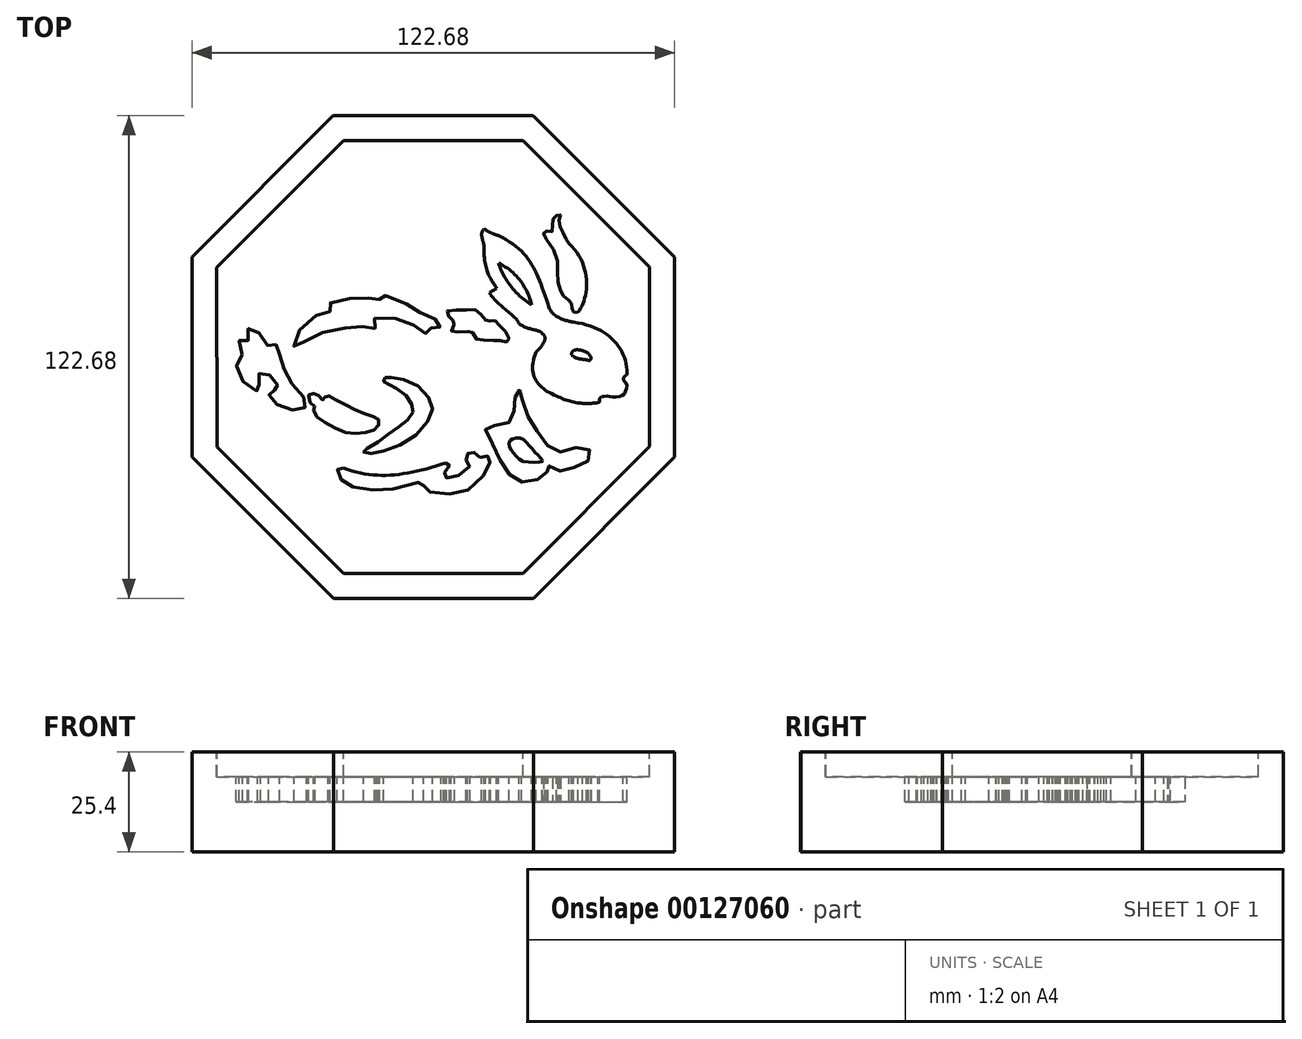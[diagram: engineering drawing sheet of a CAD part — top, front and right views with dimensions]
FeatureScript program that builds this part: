
annotation { "Feature Type Name" : "Feature", "Feature Type Description" : "" }
export const myFeature = defineFeature(function(context is Context, id is Id, definition is map)
    precondition{}
    {
        {
            var Q0;
            Q0=qCreatedBy(makeId("Top.planeOp"),FACE);
            var sketch = newSketch(context, id + "F0", { "sketchPlane" : qUnion([Q0])});
            skCircle(sketch, "E0.cCircle", {"center": v(0, 0) * mm, "radius": 61.32 * mm, "construction": true});
            skLineSegment(sketch, "E0.0", {"start": v(-61.3, -25.44) * mm, "end": v(-61.34, 25.36) * mm});
            skLineSegment(sketch, "E0.1", {"start": v(-61.34, 25.36) * mm, "end": v(-25.44, 61.3) * mm});
            skLineSegment(sketch, "E0.2", {"start": v(-25.44, 61.3) * mm, "end": v(25.36, 61.34) * mm});
            skLineSegment(sketch, "E0.3", {"start": v(25.36, 61.34) * mm, "end": v(61.3, 25.44) * mm});
            skLineSegment(sketch, "E0.4", {"start": v(61.3, 25.44) * mm, "end": v(61.34, -25.36) * mm});
            skLineSegment(sketch, "E0.5", {"start": v(61.34, -25.36) * mm, "end": v(25.44, -61.3) * mm});
            skLineSegment(sketch, "E0.6", {"start": v(25.44, -61.3) * mm, "end": v(-25.36, -61.34) * mm});
            skLineSegment(sketch, "E0.7", {"start": v(-25.36, -61.34) * mm, "end": v(-61.3, -25.44) * mm});
            skPoint(sketch, "E0.0.midPoint", {"position": v(-61.32, -0.04) * mm});
            skSolve(sketch);
        }
        {
            var Q0;
            Q0=qSketchRegion(id+"F0",true);
            extrude(context, id + "F1", {"entities" : qUnion([Q0]), "depth" : 25.4 * mm});
        }
        {
            var Q0;
            Q0=makeQuery(id+"F1.opExtrude","CAP_FACE",FACE,{"disambiguationData":[OSD([sQuery(id+"F0.wireOp",EDGE,"E0.0"),sQuery(id+"F0.wireOp",EDGE,"E0.1"),sQuery(id+"F0.wireOp",EDGE,"E0.2"),sQuery(id+"F0.wireOp",EDGE,"E0.3"),sQuery(id+"F0.wireOp",EDGE,"E0.4"),sQuery(id+"F0.wireOp",EDGE,"E0.5"),sQuery(id+"F0.wireOp",EDGE,"E0.6"),sQuery(id+"F0.wireOp",EDGE,"E0.7")])],"isStart":false});
            var sketch = newSketch(context, id + "F2", { "sketchPlane" : qUnion([Q0])});
            skLineSegment(sketch, "E1.0", {"start": v(-54.96, -22.8) * mm, "end": v(-54.99, 22.73) * mm});
            skLineSegment(sketch, "E1.1", {"start": v(-22.73, -54.99) * mm, "end": v(-54.96, -22.8) * mm});
            skLineSegment(sketch, "E1.2", {"start": v(-54.99, 22.73) * mm, "end": v(-22.8, 54.96) * mm});
            skLineSegment(sketch, "E1.3", {"start": v(22.8, -54.96) * mm, "end": v(-22.73, -54.99) * mm});
            skLineSegment(sketch, "E1.4", {"start": v(-22.8, 54.96) * mm, "end": v(22.73, 54.99) * mm});
            skLineSegment(sketch, "E1.5", {"start": v(22.73, 54.99) * mm, "end": v(54.96, 22.8) * mm});
            skLineSegment(sketch, "E1.6", {"start": v(54.96, 22.8) * mm, "end": v(54.99, -22.73) * mm});
            skLineSegment(sketch, "E1.7", {"start": v(54.99, -22.73) * mm, "end": v(22.8, -54.96) * mm});
            skSolve(sketch);
        }
        {
            var Q0;
            Q0=qSketchRegion(id+"F2",true);
            extrude(context, id + "F3", {"entities" : qUnion([Q0]), "operationType" : NewBodyOperationType.REMOVE, "oppositeDirection" : true, "depth" : 6.35 * mm});
        }
        {
            var Q0;
            Q0=makeQuery(id+"F3.boolean.opBoolean","COPY",FACE,{"derivedFrom":makeQuery(id+"F3.opExtrude","CAP_FACE",FACE,{"disambiguationData":[OSD([sQuery(id+"F2.wireOp",EDGE,"E1.0"),sQuery(id+"F2.wireOp",EDGE,"E1.1"),sQuery(id+"F2.wireOp",EDGE,"E1.2"),sQuery(id+"F2.wireOp",EDGE,"E1.3"),sQuery(id+"F2.wireOp",EDGE,"E1.4"),sQuery(id+"F2.wireOp",EDGE,"E1.5"),sQuery(id+"F2.wireOp",EDGE,"E1.6"),sQuery(id+"F2.wireOp",EDGE,"E1.7")])],"isStart":false})});
            var sketch = newSketch(context, id + "F4", { "sketchPlane" : qUnion([Q0])});
            skFitSpline(sketch, "E2", {"points": [v(16.6, 23.85) * mm, v(25, 13.25) * mm], "startDerivative": vector(13.68, -6.4) * mm, "endDerivative": vector(3.38, -13.15) * mm});
            skFitSpline(sketch, "E3", {"points": [v(16.6, 23.85) * mm, v(25, 13.25) * mm], "startDerivative": vector(3.38, -11.2) * mm, "endDerivative": vector(12.61, -7.28) * mm});
            skFitSpline(sketch, "E4", {"points": [v(12.87, 32.6) * mm, v(16.54, 30.9) * mm], "startDerivative": vector(4.26, -2.66) * mm, "endDerivative": vector(3.55, -0.53) * mm});
            skFitSpline(sketch, "E5", {"points": [v(16.54, 30.9) * mm, v(29.1, 13.42) * mm], "startDerivative": vector(24.52, -12.44) * mm, "endDerivative": vector(8.7, -26.3) * mm});
            skFitSpline(sketch, "E6", {"points": [v(29.1, 13.42) * mm, v(35.6, 8.86) * mm], "startDerivative": vector(2.49, -10.13) * mm, "endDerivative": vector(6.93, -1.42) * mm});
            skFitSpline(sketch, "E7", {"points": [v(12.87, 32.6) * mm, v(12.87, 28.05) * mm], "startDerivative": vector(-3.9, -4.62) * mm, "endDerivative": vector(0, -4.56) * mm});
            skFitSpline(sketch, "E8", {"points": [v(12.87, 28.05) * mm, v(16.12, 17.45) * mm], "startDerivative": vector(0, -19) * mm, "endDerivative": vector(5.33, -8.35) * mm});
            skFitSpline(sketch, "E9", {"points": [v(16.12, 17.45) * mm, v(14.23, 16.38) * mm], "startDerivative": vector(-1.9, -1.07) * mm, "endDerivative": vector(-1.9, -1.07) * mm});
            skFitSpline(sketch, "E10", {"points": [v(14.23, 16.38) * mm, v(21.8, 8.5) * mm], "startDerivative": vector(6.57, -10.84) * mm, "endDerivative": vector(3.38, -7.28) * mm});
            skFitSpline(sketch, "E11", {"points": [v(21.8, 8.5) * mm, v(27.6, 5.96) * mm], "startDerivative": vector(5.5, -4.97) * mm, "endDerivative": vector(0.36, -3.02) * mm});
            skFitSpline(sketch, "E12", {"points": [v(27.6, 5.96) * mm, v(26.13, 1.28) * mm], "startDerivative": vector(3.38, -1.78) * mm, "endDerivative": vector(-8.35, -8) * mm});
            skFitSpline(sketch, "E13", {"points": [v(26.13, 1.28) * mm, v(31.28, -9.85) * mm], "startDerivative": vector(-7.28, -16.88) * mm, "endDerivative": vector(14.74, -5.68) * mm});
            skFitSpline(sketch, "E14", {"points": [v(35.6, 8.86) * mm, v(49.25, -4.16) * mm], "startDerivative": vector(27.07, -3.62) * mm, "endDerivative": vector(0.36, -19.2) * mm});
            skFitSpline(sketch, "E15", {"points": [v(31.28, -9.85) * mm, v(41.9, -11.58) * mm], "startDerivative": vector(11.45, -6.22) * mm, "endDerivative": vector(9.7, 1.41) * mm});
            skFitSpline(sketch, "E16", {"points": [v(41.9, -11.58) * mm, v(42.28, -11.32) * mm, v(42.12, -10.92) * mm, v(42.4, -10.35) * mm, v(42.97, -10.04) * mm, v(44.26, -9.98) * mm, v(46.05, -10.13) * mm, v(48.08, -9.76) * mm, v(49, -8.44) * mm, v(49.15, -6.87) * mm, v(48.37, -5.9) * mm, v(48.33, -5.2) * mm, v(48.9, -4.67) * mm, v(49.25, -4.16) * mm], "startDerivative": vector(10.5, 4.13) * mm, "endDerivative": vector(4.68, 8.85) * mm});
            skFitSpline(sketch, "E17", {"points": [v(35.16, 0.47) * mm, v(37.86, 1.66) * mm], "startDerivative": vector(-0.47, 4.33) * mm, "endDerivative": vector(4.52, -1.22) * mm});
            skFitSpline(sketch, "E18", {"points": [v(37.86, 1.66) * mm, v(39.43, -0.85) * mm], "startDerivative": vector(8.19, -2.54) * mm, "endDerivative": vector(-2.82, 0.75) * mm});
            skFitSpline(sketch, "E19", {"points": [v(35.16, 0.47) * mm, v(39.43, -0.85) * mm], "startDerivative": vector(3.39, -3.58) * mm, "endDerivative": vector(2.26, -0.94) * mm});
            skFitSpline(sketch, "E20", {"points": [v(36.78, 11.4) * mm, v(34.5, 28.77) * mm], "startDerivative": vector(8.06, 10.18) * mm, "endDerivative": vector(-18.13, 16.56) * mm});
            skFitSpline(sketch, "E21", {"points": [v(36.78, 11.4) * mm, v(36, 11.4) * mm, v(35.58, 11.4) * mm, v(35.17, 12.62) * mm, v(35.1, 13.63) * mm, v(34.61, 14.34) * mm, v(33.23, 15.34) * mm, v(32.26, 17.06) * mm, v(31.52, 20.83) * mm, v(31.1, 26.16) * mm, v(28.12, 30.94) * mm, v(28.12, 31.65) * mm, v(28.87, 32.02) * mm, v(30.1, 31.83) * mm, v(30.25, 33.62) * mm, v(30.47, 35.12) * mm, v(31.22, 35.94) * mm, v(32.23, 36.2) * mm, v(32.08, 35.53) * mm, v(32.08, 33.74) * mm, v(32.71, 32.06) * mm, v(33.76, 30) * mm, v(34.5, 28.77) * mm], "startDerivative": vector(-23.61, 2.15) * mm, "endDerivative": vector(16.72, -26.25) * mm});
            skFitSpline(sketch, "E22", {"points": [v(15.3, 4.19) * mm, v(16.63, 4.28) * mm, v(18.23, 3.85) * mm, v(18.92, 4.02) * mm, v(19.22, 4.68) * mm, v(18.4, 6.51) * mm, v(16.63, 8.24) * mm, v(15.73, 9.2) * mm, v(14.87, 9.34) * mm, v(14, 8.97) * mm, v(13.2, 9.44) * mm, v(12.28, 10.6) * mm, v(10.65, 12) * mm, v(8.29, 11.96) * mm, v(4.67, 11.9) * mm, v(3.34, 11.5) * mm, v(4, 10.17) * mm, v(4.93, 9.27) * mm, v(5.43, 8.74) * mm, v(4.97, 7.9) * mm, v(4.67, 6.38) * mm, v(7, 6.44) * mm, v(9.55, 6.41) * mm, v(9.95, 6.28) * mm, v(10.75, 4.72) * mm, v(12.18, 4.35) * mm, v(15.3, 4.19) * mm]});
            skFitSpline(sketch, "E23", {"points": [v(22.8, -26.48) * mm, v(20.72, -24.8) * mm, v(19.57, -23.24) * mm, v(19.35, -21.51) * mm, v(20.46, -20.76) * mm, v(22.32, -20.67) * mm, v(24.4, -22.5) * mm, v(26.13, -24.44) * mm, v(27.51, -25.9) * mm, v(27.73, -26.53) * mm, v(27.16, -26.66) * mm, v(22.8, -26.48) * mm]});
            skFitSpline(sketch, "E24", {"points": [v(20.73, -10.33) * mm, v(20.9, -9.1) * mm, v(21.17, -8.52) * mm, v(22.36, -8.6) * mm, v(22.36, -9.18) * mm, v(22.76, -11.44) * mm, v(23.7, -14.37) * mm, v(25.12, -16.55) * mm, v(26.8, -19.65) * mm, v(28.66, -22.27) * mm, v(30.62, -23.56) * mm, v(32.7, -24.09) * mm, v(35.27, -23.38) * mm, v(37.63, -22.76) * mm, v(39.44, -23.42) * mm, v(40.2, -24.8) * mm, v(39.49, -26.3) * mm, v(37.8, -27.33) * mm, v(35.32, -28.26) * mm, v(33.28, -28.88) * mm, v(31.06, -28.8) * mm, v(29.77, -27.86) * mm, v(29.15, -27.55) * mm, v(28.76, -27.65) * mm, v(28.89, -28.73) * mm, v(28.72, -29.46) * mm, v(27.64, -30.35) * mm, v(25.73, -31.55) * mm, v(23, -31.9) * mm, v(20.74, -31.06) * mm, v(19.2, -29.66) * mm, v(17.35, -26.97) * mm, v(16.15, -24.4) * mm, v(14.65, -21.25) * mm, v(13.32, -18.94) * mm, v(13.45, -17.79) * mm, v(14.34, -17.48) * mm, v(16.5, -17.3) * mm, v(18.8, -16.95) * mm, v(20.2, -15.66) * mm, v(20.5, -14.02) * mm, v(20.68, -12.17) * mm, v(20.73, -10.33) * mm]});
            skFitSpline(sketch, "E25", {"points": [v(3.12, -26.91) * mm, v(-22.85, -28.22) * mm], "startDerivative": vector(-28.93, -9.6) * mm, "endDerivative": vector(-25.14, 9.6) * mm});
            skFitSpline(sketch, "E26", {"points": [v(-22.85, -28.22) * mm, v(-23.72, -27.82) * mm, v(-24.23, -28.22) * mm, v(-24.35, -29.8) * mm, v(-23.36, -31.22) * mm, v(-20.95, -32.8) * mm, v(-15.58, -33.75) * mm, v(-9.53, -33.43) * mm, v(-2.61, -31.7) * mm, v(-2.46, -32) * mm, v(-2.46, -32.84) * mm, v(-2.38, -33.75) * mm, v(1.65, -34.58) * mm, v(6.67, -34.58) * mm, v(11.5, -31.61) * mm, v(14.06, -27.5) * mm, v(14.5, -26.32) * mm, v(14.42, -25.4) * mm, v(13.5, -25.17) * mm, v(12.64, -25.49) * mm, v(11.89, -25.49) * mm, v(11.26, -25.25) * mm, v(10.66, -24.5) * mm, v(9.64, -23.87) * mm, v(9, -24.03) * mm, v(8.73, -24.82) * mm, v(8.69, -25.6) * mm, v(8.33, -26.16) * mm, v(9.12, -26.48) * mm, v(9.32, -27.39) * mm, v(7.62, -29.56) * mm, v(4.74, -30.5) * mm, v(3.23, -30.7) * mm, v(2.6, -30.43) * mm, v(2.68, -29.72) * mm, v(3.47, -28.69) * mm, v(3.99, -27.86) * mm, v(4.14, -26.91) * mm, v(3.83, -26.67) * mm, v(3.12, -26.91) * mm], "startDerivative": vector(-45.93, 29.93) * mm, "endDerivative": vector(-42.98, -21.04) * mm});
            skFitSpline(sketch, "E27", {"points": [v(-10.66, -5.21) * mm, v(-11.81, -5.1) * mm, v(-12.56, -5.51) * mm, v(-12.67, -6.07) * mm, v(-12.33, -6.4) * mm, v(-11.07, -7.04) * mm, v(-9.16, -8.12) * mm, v(-6.33, -10.43) * mm, v(-5.28, -12.7) * mm, v(-5.32, -14.5) * mm, v(-7.45, -16.74) * mm, v(-10.62, -19.09) * mm, v(-14.76, -22.07) * mm, v(-17.52, -23.68) * mm, v(-17.74, -24.05) * mm, v(-16.89, -24.5) * mm, v(-14.01, -24.16) * mm, v(-5.92, -21) * mm, v(-0.58, -14.72) * mm, v(-0.77, -10.88) * mm, v(-5.73, -6.3) * mm, v(-10.66, -5.21) * mm]});
            skFitSpline(sketch, "E28", {"points": [v(-22.3, -19.16) * mm, v(-18.6, -19.35) * mm, v(-15.54, -18.72) * mm, v(-14.13, -17.7) * mm, v(-13.68, -16.37) * mm, v(-14.16, -15.62) * mm, v(-16.25, -14.87) * mm, v(-19.72, -13.53) * mm, v(-22.78, -11.93) * mm, v(-26.14, -10.14) * mm, v(-26.96, -9.76) * mm, v(-27.55, -10.21) * mm, v(-27.78, -10.88) * mm, v(-28.45, -10.7) * mm, v(-29.42, -9.5) * mm, v(-30.31, -9.28) * mm, v(-31.5, -9.35) * mm, v(-31.5, -11.14) * mm, v(-30.5, -12.3) * mm, v(-30.02, -12.78) * mm, v(-30.35, -13.6) * mm, v(-29.57, -15.13) * mm, v(-26.44, -17.15) * mm, v(-22.3, -19.16) * mm]});
            skFitSpline(sketch, "E29", {"points": [v(-48.54, 0.58) * mm, v(-49.9, -0.44) * mm, v(-49.66, -3.4) * mm, v(-48.57, -5.9) * mm, v(-45.79, -8) * mm, v(-44.45, -8.71) * mm, v(-43.92, -8.3) * mm, v(-44.28, -7.06) * mm, v(-44.63, -5.72) * mm, v(-44.38, -4.38) * mm, v(-43.5, -3.75) * mm, v(-42.02, -4.31) * mm, v(-40.33, -5.5) * mm, v(-39.52, -7.2) * mm, v(-39.03, -8.3) * mm, v(-39.9, -8.4) * mm, v(-41.21, -8.5) * mm, v(-41.81, -9.14) * mm, v(-41.74, -9.66) * mm, v(-41.42, -10.4) * mm, v(-39.6, -12.16) * mm, v(-36.81, -13.22) * mm, v(-34.45, -13.47) * mm, v(-32.87, -12.97) * mm, v(-32.16, -12.13) * mm, v(-32.52, -10.9) * mm, v(-34.6, -8.3) * mm, v(-36.32, -6.18) * mm, v(-37.8, -3.36) * mm, v(-38.75, -0.5) * mm, v(-39.1, 1.04) * mm, v(-39.24, 2.2) * mm, v(-40.33, 3.3) * mm, v(-41.74, 3.01) * mm, v(-41.88, 2.73) * mm, v(-42.87, 4.35) * mm, v(-44.24, 6.04) * mm, v(-45.93, 6.85) * mm, v(-46.99, 7.2) * mm, v(-47.02, 5.16) * mm, v(-47.06, 4.17) * mm, v(-48.29, 4.35) * mm, v(-49.24, 4.53) * mm, v(-48.82, 2.3) * mm, v(-48.54, 0.58) * mm]});
            skFitSpline(sketch, "E30", {"points": [v(-14.9, 9.97) * mm, v(-10.7, 10.05) * mm, v(-6.59, 8.86) * mm, v(-3.52, 7.15) * mm, v(-2.17, 6.06) * mm, v(-1.54, 6.1) * mm, v(-0.92, 6.35) * mm, v(-0.72, 7.19) * mm, v(0, 7.48) * mm, v(1.23, 7.19) * mm, v(1.64, 7.54) * mm, v(1.92, 8.2) * mm, v(1.36, 9.05) * mm, v(-0.92, 10.25) * mm, v(-3.26, 11.23) * mm, v(-5.22, 12.6) * mm, v(-8.78, 14.36) * mm, v(-13.1, 15.7) * mm, v(-14, 15.32) * mm, v(-13.83, 15.09) * mm, v(-13.93, 14.2) * mm, v(-14.28, 14.52) * mm, v(-17.33, 14.94) * mm, v(-20.88, 14.93) * mm, v(-25.16, 14.3) * mm, v(-26.7, 13) * mm, v(-26.53, 12.42) * mm, v(-26.23, 11.62) * mm, v(-27.53, 11.34) * mm, v(-30.2, 10.28) * mm, v(-33.87, 6.9) * mm, v(-35.28, 3.38) * mm, v(-35.3, 2.62) * mm, v(-34.13, 3.13) * mm, v(-33, 3.77) * mm, v(-29.06, 5.91) * mm, v(-23.35, 7.26) * mm, v(-20.02, 7.59) * mm, v(-17.26, 7.62) * mm, v(-15.72, 7.19) * mm, v(-14.65, 7.39) * mm, v(-14.5, 8.4) * mm, v(-14.9, 9.97) * mm]});
            skSolve(sketch);
        }
        {
            var Q0;
            Q0 = qSketchRegion(id + "F4", true);
            extrude(context, id + "F5", {"entities" : qUnion([Q0]), "operationType" : NewBodyOperationType.REMOVE, "oppositeDirection" : true, "depth" : 6.35 * mm});
        }
    });
